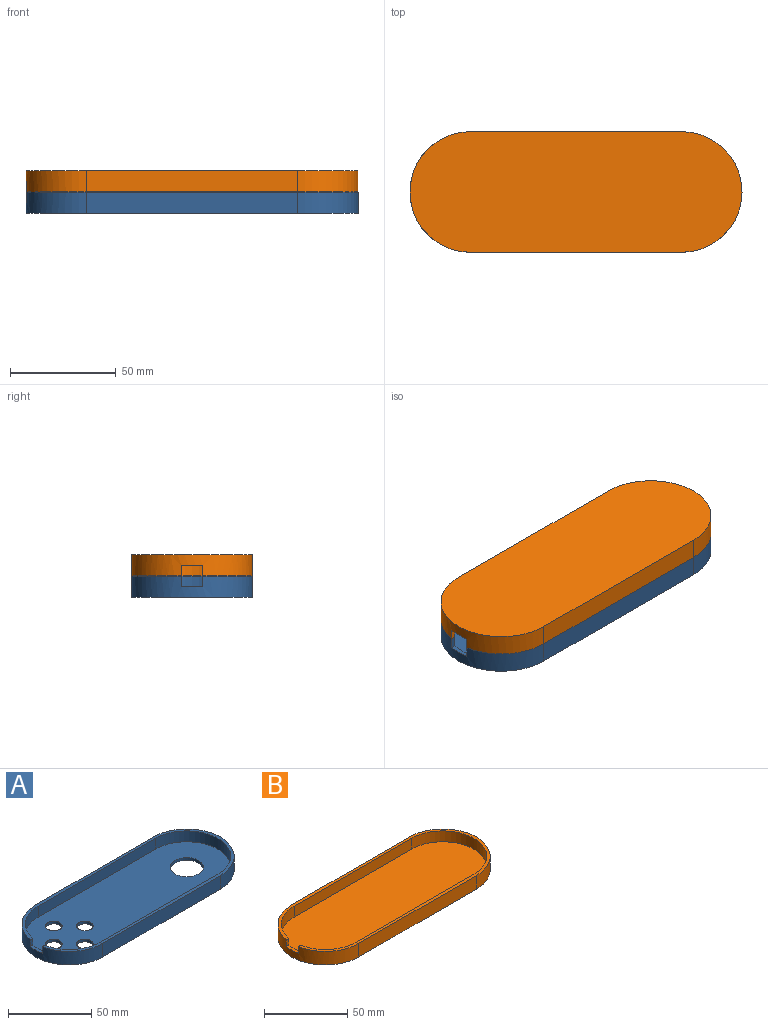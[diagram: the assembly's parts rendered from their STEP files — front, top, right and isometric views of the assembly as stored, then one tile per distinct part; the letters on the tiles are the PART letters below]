
ASSEMBLY  parts=2 mates=1
PART A: 19 faces, bbox 157x57x10 mm
  f0: plane 5x2.03mm, normal (0,1,0), area 10.2mm2, adj f4,f6,f10,f12
  f1: plane 100x10mm, normal (0,-1,0), area 1000mm2, adj f2,f4,f10,f11
  f2: cylinder r=28.5mm len=57mm, axis (0,0,-1), area 895.4mm2, adj f1,f3,f10,f11
  f3: plane 100x10mm, normal (0,1,0), area 1000mm2, adj f2,f4,f10,f11
  f4: cylinder r=28.5mm len=57mm, axis (0,0,-1), area 845.1mm2, adj f0,f1,f3,f5,f10,f11,f12
  f5: plane 5x2.03mm, normal (0,-1,0), area 10.2mm2, adj f4,f6,f10,f12
  f6: cylinder r=26.5mm len=53mm, axis (0,0,-1), area 615.7mm2, adj f0,f5,f7,f9,f10,f12,f18
  f7: plane 100x8mm, normal (0,-1,0), area 800mm2, adj f6,f8,f10,f18
  f8: cylinder r=26.5mm len=53mm, axis (0,0,-1), area 666mm2, adj f7,f9,f10,f18
  f9: plane 100x8mm, normal (0,1,0), area 800mm2, adj f6,f8,f10,f18
  f10: plane 156.56x57mm, normal (0,0,1), area 725.5mm2, adj f0,f1,f2,f3,f4,f5,f6,f7
  f11: plane 157x57mm, normal (0,0,-1), area 7623.4mm2, adj f1,f2,f3,f4,f13,f14,f15,f16
  f12: plane 10x2.48mm, normal (0,0,1), area 20.1mm2, adj f0,f4,f5,f6
  f13: cylinder r=5mm len=10mm, axis (0,0,-1), area 62.8mm2, adj f11,f18
  f14: cylinder r=5mm len=10mm, axis (0,0,-1), area 62.8mm2, adj f11,f18
  f15: cylinder r=5mm len=10mm, axis (0,0,-1), area 62.8mm2, adj f11,f18
  f16: cylinder r=5mm len=10mm, axis (0,0,-1), area 62.8mm2, adj f11,f18
  f17: cylinder r=10mm len=20mm, axis (0,0,-1), area 125.7mm2, adj f11,f18
  f18: plane 153x53mm, normal (0,0,1), area 6877.9mm2, adj f6,f7,f8,f9,f13,f14,f15,f16
PART B: 14 faces, bbox 157x57x10 mm
  f0: cylinder r=28.5mm len=57mm, axis (0,0,-1), area 895.4mm2, adj f1,f9,f10,f11
  f1: plane 100x10mm, normal (0,1,0), area 1000mm2, adj f0,f2,f10,f11
  f2: cylinder r=28.5mm len=57mm, axis (0,0,-1), area 845.1mm2, adj f1,f3,f8,f9,f10,f11,f12
  f3: plane 5x2.03mm, normal (0,-1,0), area 10.2mm2, adj f2,f4,f10,f12
  f4: cylinder r=26.5mm len=53mm, axis (0,0,-1), area 615.7mm2, adj f3,f5,f7,f8,f10,f12,f13
  f5: plane 100x8mm, normal (0,-1,0), area 800mm2, adj f4,f6,f10,f13
  f6: cylinder r=26.5mm len=53mm, axis (0,0,-1), area 666mm2, adj f5,f7,f10,f13
  f7: plane 100x8mm, normal (0,1,0), area 800mm2, adj f4,f6,f10,f13
  f8: plane 5x2.03mm, normal (0,1,0), area 10.2mm2, adj f2,f4,f10,f12
  f9: plane 100x10mm, normal (0,-1,0), area 1000mm2, adj f0,f2,f10,f11
  f10: plane 156.56x57mm, normal (0,0,1), area 725.5mm2, adj f0,f1,f2,f3,f4,f5,f6,f7
  f11: plane 157x57mm, normal (0,0,-1), area 8251.8mm2, adj f0,f1,f2,f9
  f12: plane 10x2.48mm, normal (0,0,1), area 20.1mm2, adj f2,f3,f4,f8
  f13: plane 153x53mm, normal (0,0,1), area 7506.2mm2, adj f4,f5,f6,f7
PLACE A t=(-1.86,15.99,20.6)mm
PLACE B rot(axis=(1,0,0),180deg) t=(-1.86,15.99,40.6)mm
MATE fastened B.f10 <-> A.f10  axis (0,0,-1) through (0.28,15.99,30.6)mm
